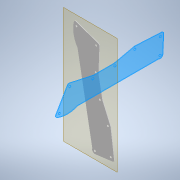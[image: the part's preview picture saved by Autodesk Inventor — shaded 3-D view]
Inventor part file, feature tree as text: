
AUTODESK INVENTOR PART (.ipt)
format: ipt  version: 2020 (Build 240168000, 168)  size: 142,848 bytes
history: native  units: mm
features: reference x5, other x3, plane x1, extrude x1, sketch x1
ambient origin geometry x8: Origin, YZ Plane, XZ Plane, XY Plane, X Axis, Y Axis, Z Axis, Center Point
bodies: Solid1 (feature_tree)
feature tree (11):
  plane  "Work Plane1"
  extrude  "Extrusion1"  [1 undecoded]
  sketch  "Sketch1"  dims[d0=1.0mm d1=0.0mm]
  reference  "Reference1"
  reference  "Reference2"
  reference  "Reference3"
  reference  "Reference4"
  reference  "Reference5"
  other  "Kauri Assembly.iam"
  other  "Kauri side plate:2"
  other  "Kauri mid plate v2:1"
note: 1 required parameter value undecoded (feature->parameter linkage not recoverable at this tier; creation-order binding heuristic only, values carry confidence <= 0.55)
